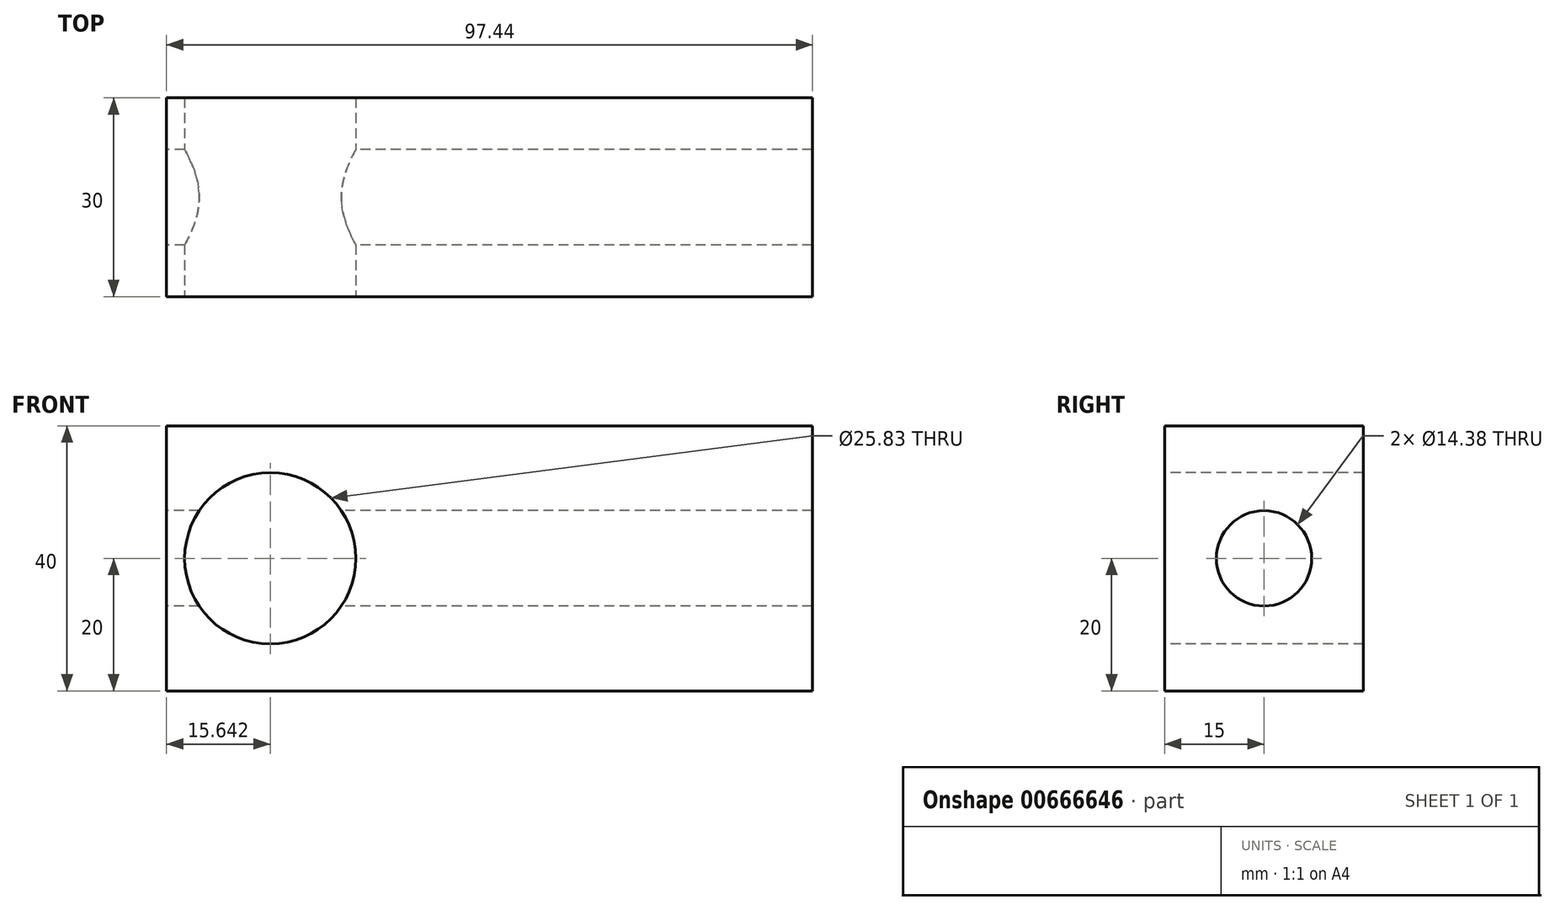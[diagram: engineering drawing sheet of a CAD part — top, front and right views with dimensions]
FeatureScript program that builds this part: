
annotation { "Feature Type Name" : "Feature", "Feature Type Description" : "" }
export const myFeature = defineFeature(function(context is Context, id is Id, definition is map)
    precondition{}
    {
        {
            var Q0;
            Q0=qCreatedBy(makeId("Front.planeOp"),FACE);
            var sketch = newSketch(context, id + "F0", { "sketchPlane" : qUnion([Q0])});
            skLineSegment(sketch, "E0.bottom", {"start": v(48.72, 20) * mm, "end": v(-48.72, 20) * mm});
            skLineSegment(sketch, "E0.top", {"start": v(48.72, -20) * mm, "end": v(-48.72, -20) * mm});
            skLineSegment(sketch, "E0.left", {"start": v(48.72, 20) * mm, "end": v(48.72, -20) * mm});
            skLineSegment(sketch, "E0.right", {"start": v(-48.72, 20) * mm, "end": v(-48.72, -20) * mm});
            skPoint(sketch, "E0.middle", {"position": v(0, 0) * mm});
            skSolve(sketch);
        }
        {
            var Q0;
            Q0=makeQuery(id+"F0.imprint","IMPRINT",FACE,{"disambiguationData":[TD([[makeQuery(id+"F0.imprint","IMPRINT",EDGE,{"derivedFrom":sQuery(id+"F0.wireOp",EDGE,"E0.bottom")}),1.0]])]});
            extrude(context, id + "F1", {"entities" : qUnion([Q0]), "endBound" : BoundingType.SYMMETRIC, "depth" : 30 * mm, "offsetDistance" : 25.4 * mm});
        }
        {
            var Q0;
            Q0=makeQuery(id+"F1.opExtrude","CAP_FACE",FACE,{"disambiguationData":[OSD([sQuery(id+"F0.wireOp",EDGE,"E0.bottom"),sQuery(id+"F0.wireOp",EDGE,"E0.top"),sQuery(id+"F0.wireOp",EDGE,"E0.left"),sQuery(id+"F0.wireOp",EDGE,"E0.right")])],"isStart":false});
            var sketch = newSketch(context, id + "F2", { "sketchPlane" : qUnion([Q0])});
            skCircle(sketch, "E1", {"center": v(-33.08, 0) * mm, "radius": 12.91 * mm});
            skSolve(sketch);
        }
        {
            var Q0;
            Q0=makeQuery(id+"F2.imprint","IMPRINT",FACE,{"disambiguationData":[TD([[makeQuery(id+"F2.imprint","IMPRINT",EDGE,{"derivedFrom":sQuery(id+"F2.wireOp",EDGE,"E1")}),1.0]])]});
            extrude(context, id + "F3", {"entities" : qUnion([Q0]), "operationType" : NewBodyOperationType.REMOVE, "oppositeDirection" : true, "depth" : 100 * mm, "offsetDistance" : 25 * mm});
        }
        {
            var Q0;
            Q0=makeQuery(id+"F1.opExtrude","SWEPT_FACE",FACE,{"disambiguationData":[OSD([sQuery(id+"F0.wireOp",EDGE,"E0.right")])]});
            var sketch = newSketch(context, id + "F4", { "sketchPlane" : qUnion([Q0])});
            skCircle(sketch, "E2", {"center": v(0, 0) * mm, "radius": 7.2 * mm});
            skSolve(sketch);
        }
        {
            var Q0;
            Q0=makeQuery(id+"F4.imprint","IMPRINT",FACE,{"disambiguationData":[TD([[makeQuery(id+"F4.imprint","IMPRINT",EDGE,{"derivedFrom":sQuery(id+"F4.wireOp",EDGE,"E2")}),1.0]])]});
            extrude(context, id + "F5", {"entities" : qUnion([Q0]), "operationType" : NewBodyOperationType.REMOVE, "oppositeDirection" : true, "depth" : 1000 * mm, "offsetDistance" : 25 * mm});
        }
    });
